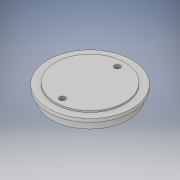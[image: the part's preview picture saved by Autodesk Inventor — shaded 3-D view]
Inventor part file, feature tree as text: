
AUTODESK INVENTOR PART (.ipt)
format: ipt  version: 2017 (Build 210142000, 142)  size: 132,608 bytes
history: native  units: in
note: dims shown in document units (in); Inventor stores cm internally (conversion verified against a paired STEP export)
features: sketch x2, revolve x1, hole x1
ambient origin geometry x8: Origin, YZ Plane, XZ Plane, XY Plane, X Axis, Y Axis, Z Axis, Center Point
bodies: Solid1 (feature_tree)
feature tree (4):
  revolve  "Revolution1"  [1 undecoded]
  hole  "Hole1"  [1 undecoded]
  sketch  "Sketch1"  dims[d1=0.5in d3=0.147in d5=0.195in d8=0.691in d9=1.668in]
  sketch  "Sketch2"  dims[d10=1.814in d11=0.062in d12=1.4975in d13=90.0deg d14=2.376in d15=0.25in d16=0.75in d17=0.375in d18=0.25in d19=0.5635in d20=0.4in d21=0.0in]
note: 2 required parameter values undecoded (feature->parameter linkage not recoverable at this tier; creation-order binding heuristic only, values carry confidence <= 0.55)